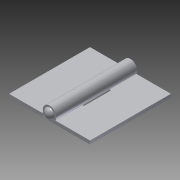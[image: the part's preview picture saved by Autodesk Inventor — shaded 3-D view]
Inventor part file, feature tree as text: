
AUTODESK INVENTOR PART (.ipt)
format: ipt  version: 2014 (Build 180170000, 170)  size: 133,632 bytes
history: native  units: in
note: dims shown in document units (in); Inventor stores cm internally (conversion verified against a paired STEP export)
features: imported_body x3, extrude x2, revolve x1, other x1
ambient origin geometry x8: Origin, YZ Plane, XZ Plane, XY Plane, X Axis, Y Axis, Z Axis, Center Point
bodies: Body1 (feature_tree), Body2 (feature_tree), Body3 (feature_tree)
feature tree (7):
  revolve  "Revolve1"  [1 undecoded]
  other  "1609A1201"
  extrude  "Extrude4"  [1 undecoded]
  extrude  "Extrude5"  [1 undecoded]
  imported_body  "Base1"
  imported_body  "Base2"
  imported_body  "Base3"
note: 3 required parameter values undecoded (feature->parameter linkage not recoverable at this tier; creation-order binding heuristic only, values carry confidence <= 0.55)
